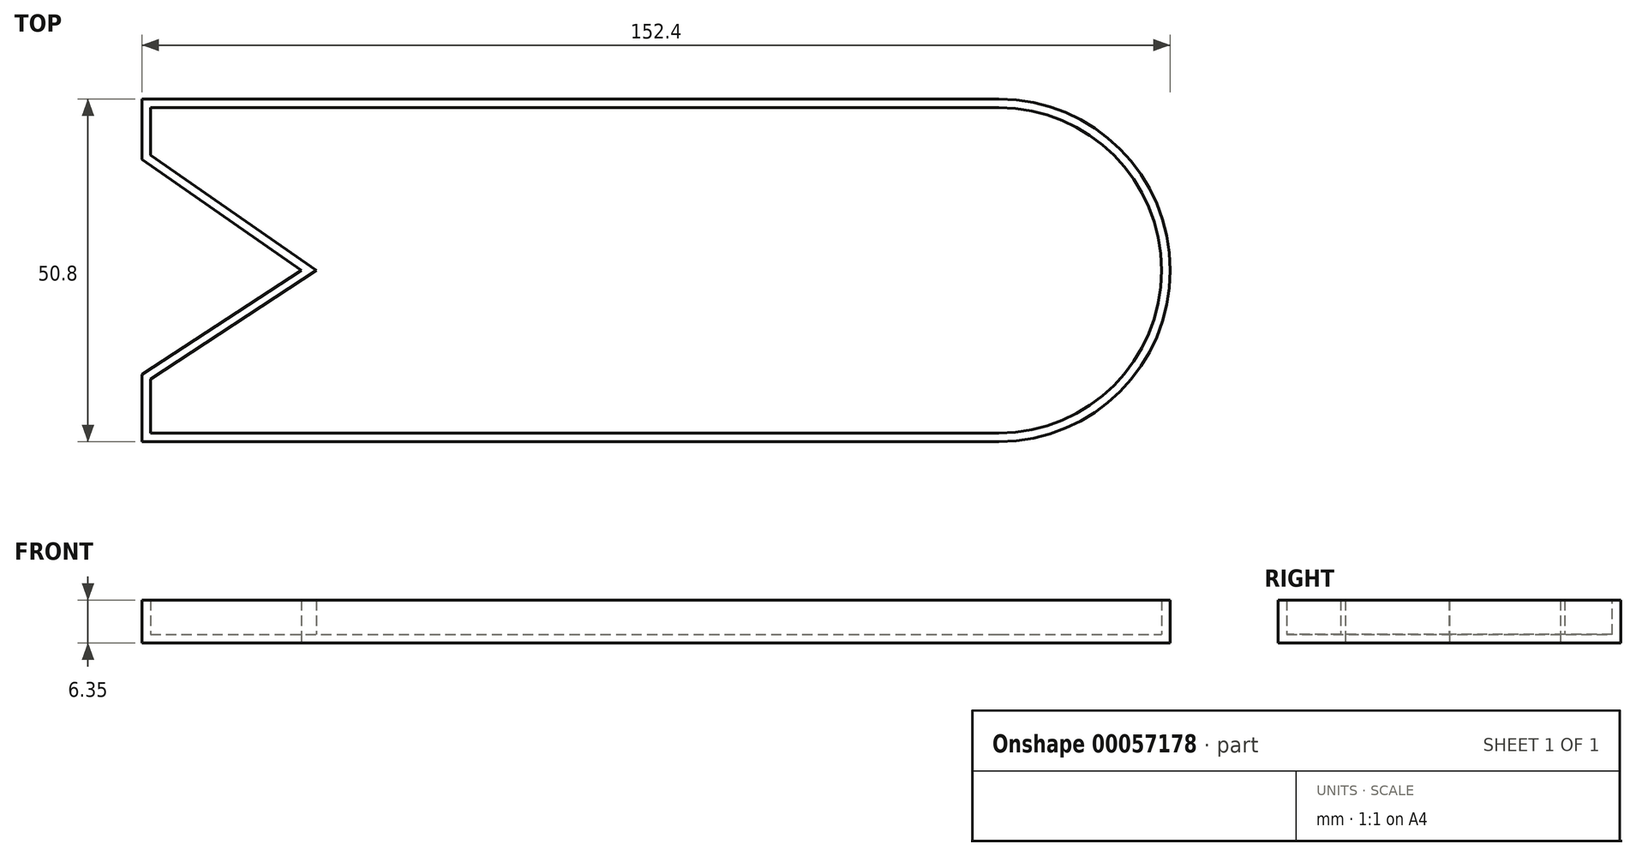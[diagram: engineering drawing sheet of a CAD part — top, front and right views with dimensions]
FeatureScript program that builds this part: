
annotation { "Feature Type Name" : "Feature", "Feature Type Description" : "" }
export const myFeature = defineFeature(function(context is Context, id is Id, definition is map)
    precondition{}
    {
        {
            var Q0;
            Q0=qCreatedBy(makeId("Top.planeOp"),FACE);
            var sketch = newSketch(context, id + "F0", { "sketchPlane" : qUnion([Q0])});
            skLineSegment(sketch, "E0.rect.bottom", {"start": v(-63.5, 25.4) * mm, "end": v(63.5, 25.4) * mm});
            skLineSegment(sketch, "E0.rect.top", {"start": v(-63.5, -25.4) * mm, "end": v(63.5, -25.4) * mm});
            skLineSegment(sketch, "E0.rect.left", {"start": v(-63.5, 25.4) * mm, "end": v(-63.5, -25.4) * mm});
            skLineSegment(sketch, "E0.rect.right", {"start": v(63.5, 25.4) * mm, "end": v(63.5, -25.4) * mm});
            skPoint(sketch, "E0.rect.middle", {"position": v(0, 0) * mm});
            skLineSegment(sketch, "E1", {"start": v(-63.5, 16.44) * mm, "end": v(-39.9, 0) * mm});
            skLineSegment(sketch, "E2", {"start": v(-39.9, 0) * mm, "end": v(-63.5, -15.43) * mm});
            skArc(sketch, "E3", {"start": v(63.5, -25.4) * mm, "mid": v(88.9, 0) * mm, "end": v(63.5, 25.4) * mm});
            skPoint(sketch, "E4", {"position": v(88.9, 0) * mm});
            skSolve(sketch);
        }
        {
            var Q0;
            Q0=makeQuery(id+"F0.imprint","IMPRINT",FACE,{"disambiguationData":[TD([[makeQuery(id+"F0.imprint","IMPRINT",EDGE,{"derivedFrom":sQuery(id+"F0.wireOp",EDGE,"E0.rect.right")}),1.0]])]});
            var Q1;
            {var subQ4=sQuery(id+"F0.wireOp",EDGE,"E0.rect.bottom");Q1=makeQuery(id+"F0.imprint","IMPRINT",FACE,{"disambiguationData":[TD([[makeQuery(id+"F0.imprint","IMPRINT",EDGE,{"derivedFrom":subQ4}),-1.0]])]});}
            extrude(context, id + "F1", {"entities" : qUnion([Q0, Q1]), "depth" : 6.35 * mm});
        }
        {
            var Q0;
            Q0=makeQuery(id+"F1.opExtrude","CAP_FACE",FACE,{"disambiguationData":[OSD([sQuery(id+"F0.wireOp",EDGE,"E0.rect.bottom"),sQuery(id+"F0.wireOp",EDGE,"E0.rect.top"),sQuery(id+"F0.wireOp",EDGE,"E0.rect.left"),sQuery(id+"F0.wireOp",EDGE,"E1"),sQuery(id+"F0.wireOp",EDGE,"E2"),sQuery(id+"F0.wireOp",EDGE,"E3")])],"isStart":false});
            shell(context, id + "F2", {"entities" : qUnion([Q0]), "thickness" : 1.27 * mm});
        }
    });
